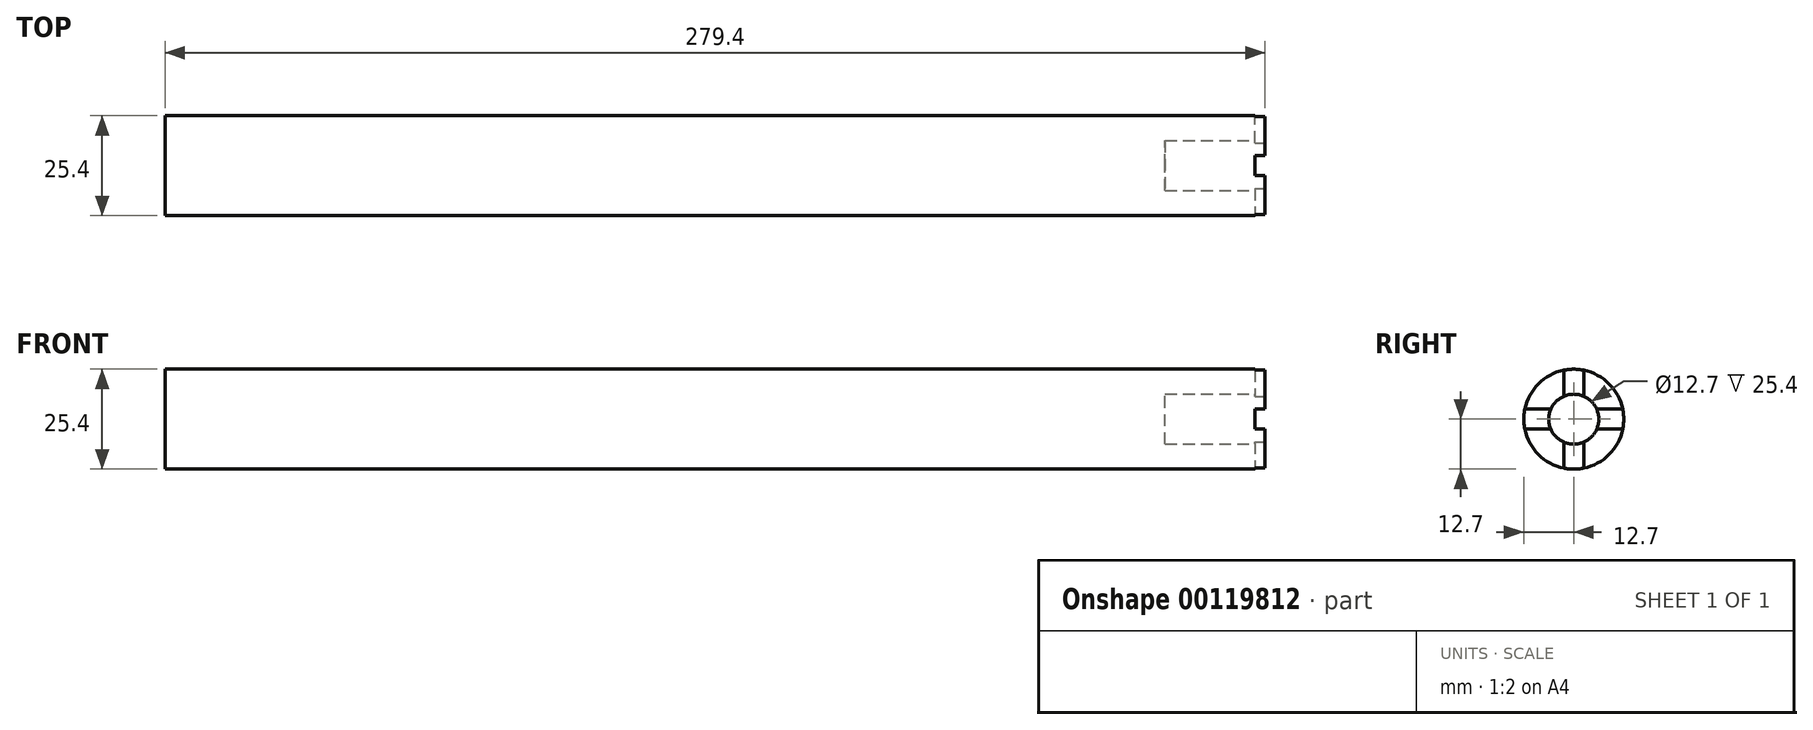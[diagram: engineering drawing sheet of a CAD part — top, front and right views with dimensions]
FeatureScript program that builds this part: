
annotation { "Feature Type Name" : "Feature", "Feature Type Description" : "" }
export const myFeature = defineFeature(function(context is Context, id is Id, definition is map)
    precondition{}
    {
        {
            var Q0;
            Q0=qCreatedBy(makeId("Right.planeOp"),FACE);
            var sketch = newSketch(context, id + "F0", { "sketchPlane" : qUnion([Q0])});
            skCircle(sketch, "E0", {"center": v(0, 0) * mm, "radius": 12.7 * mm});
            skCircle(sketch, "E1", {"center": v(0, 0) * mm, "radius": 6.35 * mm});
            skLineSegment(sketch, "E2", {"start": v(-2.54, 12.44) * mm, "end": v(-2.54, 5.82) * mm});
            skLineSegment(sketch, "E3", {"start": v(2.54, 12.44) * mm, "end": v(2.54, 5.82) * mm});
            skLineSegment(sketch, "E4", {"start": v(12.44, 2.54) * mm, "end": v(5.82, 2.54) * mm});
            skLineSegment(sketch, "E5", {"start": v(12.44, -2.54) * mm, "end": v(5.82, -2.54) * mm});
            skLineSegment(sketch, "E6", {"start": v(2.54, -12.44) * mm, "end": v(2.54, -5.82) * mm});
            skLineSegment(sketch, "E7", {"start": v(-2.54, -5.82) * mm, "end": v(-2.54, -12.44) * mm});
            skLineSegment(sketch, "E8", {"start": v(-12.44, 2.54) * mm, "end": v(-5.82, 2.54) * mm});
            skLineSegment(sketch, "E9", {"start": v(-12.44, -2.54) * mm, "end": v(-5.82, -2.54) * mm});
            skSolve(sketch);
        }
        {
            var Q0;
            Q0 = qSketchRegion(id + "F0", true);
            var Q1;
            {var subQ0=sQuery(id+"F0.wireOp",EDGE,"E1");var subQ4=makeQuery(id+"F0.imprint","INTERSECT",VERTEX,{"derivedFrom":[subQ0,sQuery(id+"F0.wireOp",EDGE,"E3")]});Q1=makeQuery(id+"F0.imprint","IMPRINT",FACE,{"disambiguationData":[TD([[makeQuery(id+"F0.imprint","IMPRINT",EDGE,{"disambiguationData":[TD([[subQ4,1.0]])],"derivedFrom":subQ0}),1.0]])]});}
            extrude(context, id + "F1", {"entities" : qUnion([Q0, Q1]), "endBound" : BoundingType.SYMMETRIC, "depth" : 207.9 * mm});
        }
        {
            var Q0;
            Q0=makeQuery(id+"F1.opExtrude","CAP_FACE",FACE,{"disambiguationData":[OSD([sQuery(id+"F0.wireOp",EDGE,"E0")])],"isStart":false});
            var sketch = newSketch(context, id + "F2", { "sketchPlane" : qUnion([Q0])});
            skCircle(sketch, "E10", {"center": v(0, 0) * mm, "radius": 6.35 * mm});
            skSolve(sketch);
        }
        {
            var Q0;
            Q0=makeQuery(id+"F2.imprint","IMPRINT",FACE,{"disambiguationData":[TD([[makeQuery(id+"F2.imprint","IMPRINT",EDGE,{"derivedFrom":sQuery(id+"F2.wireOp",EDGE,"E10")}),-1.0]])]});
            var sketch = newSketch(context, id + "F3", { "sketchPlane" : qUnion([Q0])});
            skCircle(sketch, "E11", {"center": v(0, 0) * mm, "radius": 12.7 * mm});
            skSolve(sketch);
        }
        {
            var Q0;
            Q0 = qSketchRegion(id + "F3", true);
            extrude(context, id + "F4", {"entities" : qUnion([Q0]), "operationType" : NewBodyOperationType.ADD, "depth" : 19.05 * mm});
        }
        {
            var Q0;
            Q0=makeQuery(id+"F4.opExtrude","CAP_FACE",FACE,{"disambiguationData":[OSD([sQuery(id+"F3.wireOp",EDGE,"E11")])],"isStart":false});
            var sketch = newSketch(context, id + "F5", { "sketchPlane" : qUnion([Q0])});
            skCircle(sketch, "E12", {"center": v(0, 0) * mm, "radius": 6.35 * mm});
            skCircle(sketch, "E13", {"center": v(0, 0) * mm, "radius": 12.7 * mm});
            skLineSegment(sketch, "E14", {"start": v(-2.54, 5.82) * mm, "end": v(-2.54, 12.44) * mm});
            skLineSegment(sketch, "E15", {"start": v(2.54, 5.82) * mm, "end": v(2.54, 12.44) * mm});
            skLineSegment(sketch, "E16", {"start": v(12.44, -2.54) * mm, "end": v(5.82, -2.54) * mm});
            skLineSegment(sketch, "E17", {"start": v(2.54, -5.82) * mm, "end": v(2.54, -12.44) * mm});
            skLineSegment(sketch, "E18", {"start": v(-2.54, -5.82) * mm, "end": v(-2.54, -12.44) * mm});
            skLineSegment(sketch, "E19", {"start": v(-12.44, 2.54) * mm, "end": v(-5.82, 2.54) * mm});
            skLineSegment(sketch, "E20", {"start": v(-12.44, -2.54) * mm, "end": v(-5.82, -2.54) * mm});
            skLineSegment(sketch, "E21", {"start": v(5.82, 2.54) * mm, "end": v(12.44, 2.54) * mm});
            skSolve(sketch);
        }
        {
            var Q0;
            {var subQ0=sQuery(id+"F5.wireOp",EDGE,"E12");var subQ4=makeQuery(id+"F5.imprint","INTERSECT",VERTEX,{"derivedFrom":[subQ0,sQuery(id+"F5.wireOp",EDGE,"E15")]});Q0=makeQuery(id+"F5.imprint","IMPRINT",FACE,{"disambiguationData":[TD([[makeQuery(id+"F5.imprint","IMPRINT",EDGE,{"disambiguationData":[TD([[subQ4,1.0]])],"derivedFrom":subQ0}),1.0]])]});}
            extrude(context, id + "F6", {"entities" : qUnion([Q0]), "operationType" : NewBodyOperationType.REMOVE, "oppositeDirection" : true, "depth" : 25.4 * mm});
        }
        {
            var Q0;
            Q0=makeQuery(id+"F4.opExtrude","CAP_FACE",FACE,{"disambiguationData":[OSD([sQuery(id+"F3.wireOp",EDGE,"E11")])],"isStart":false});
            var sketch = newSketch(context, id + "F7", { "sketchPlane" : qUnion([Q0])});
            skLineSegment(sketch, "E22", {"start": v(-2.54, 12.44) * mm, "end": v(-2.54, 5.82) * mm});
            skLineSegment(sketch, "E23", {"start": v(2.54, 12.44) * mm, "end": v(2.54, 5.82) * mm});
            skLineSegment(sketch, "E24", {"start": v(5.82, 2.54) * mm, "end": v(12.44, 2.54) * mm});
            skLineSegment(sketch, "E25", {"start": v(5.82, -2.54) * mm, "end": v(12.44, -2.54) * mm});
            skLineSegment(sketch, "E26", {"start": v(2.54, -5.82) * mm, "end": v(2.54, -12.44) * mm});
            skLineSegment(sketch, "E27", {"start": v(-2.54, -5.82) * mm, "end": v(-2.54, -12.44) * mm});
            skLineSegment(sketch, "E28", {"start": v(-5.82, 2.54) * mm, "end": v(-12.44, 2.54) * mm});
            skLineSegment(sketch, "E29", {"start": v(-5.82, -2.54) * mm, "end": v(-12.44, -2.54) * mm});
            skSolve(sketch);
        }
        {
            var Q0;
            Q0 = qSketchRegion(id + "F7", true);
            var Q1;
            {var subQ0=sQuery(id+"F7.wireOp",EDGE,"E22");Q1=makeQuery(id+"F7.imprint","IMPRINT",FACE,{"disambiguationData":[TD([[makeQuery(id+"F7.imprint","IMPRINT",EDGE,{"derivedFrom":subQ0}),1.0]])]});}
            var Q2;
            {var subQ0=sQuery(id+"F7.wireOp",EDGE,"E24");Q2=makeQuery(id+"F7.imprint","IMPRINT",FACE,{"disambiguationData":[TD([[makeQuery(id+"F7.imprint","IMPRINT",EDGE,{"derivedFrom":subQ0}),-1.0]])]});}
            var Q3;
            {var subQ0=sQuery(id+"F7.wireOp",EDGE,"E26");Q3=makeQuery(id+"F7.imprint","IMPRINT",FACE,{"disambiguationData":[TD([[makeQuery(id+"F7.imprint","IMPRINT",EDGE,{"derivedFrom":subQ0}),-1.0]])]});}
            var Q4;
            {var subQ0=sQuery(id+"F7.wireOp",EDGE,"E28");Q4=makeQuery(id+"F7.imprint","IMPRINT",FACE,{"disambiguationData":[TD([[makeQuery(id+"F7.imprint","IMPRINT",EDGE,{"derivedFrom":subQ0}),1.0]])]});}
            extrude(context, id + "F8", {"entities" : qUnion([Q0, Q1, Q2, Q3, Q4]), "operationType" : NewBodyOperationType.REMOVE, "oppositeDirection" : true, "depth" : 2.54 * mm});
        }
        {
            var Q0;
            Q0=makeQuery(id+"F1.opExtrude","CAP_FACE",FACE,{"disambiguationData":[OSD([sQuery(id+"F0.wireOp",EDGE,"E0")])],"isStart":true});
            var sketch = newSketch(context, id + "F9", { "sketchPlane" : qUnion([Q0])});
            skCircle(sketch, "E30", {"center": v(0, 0) * mm, "radius": 12.7 * mm});
            skSolve(sketch);
        }
        {
            var Q0;
            Q0 = qSketchRegion(id + "F9", true);
            extrude(context, id + "F10", {"entities" : qUnion([Q0]), "operationType" : NewBodyOperationType.ADD, "depth" : 52.45 * mm});
        }
    });
